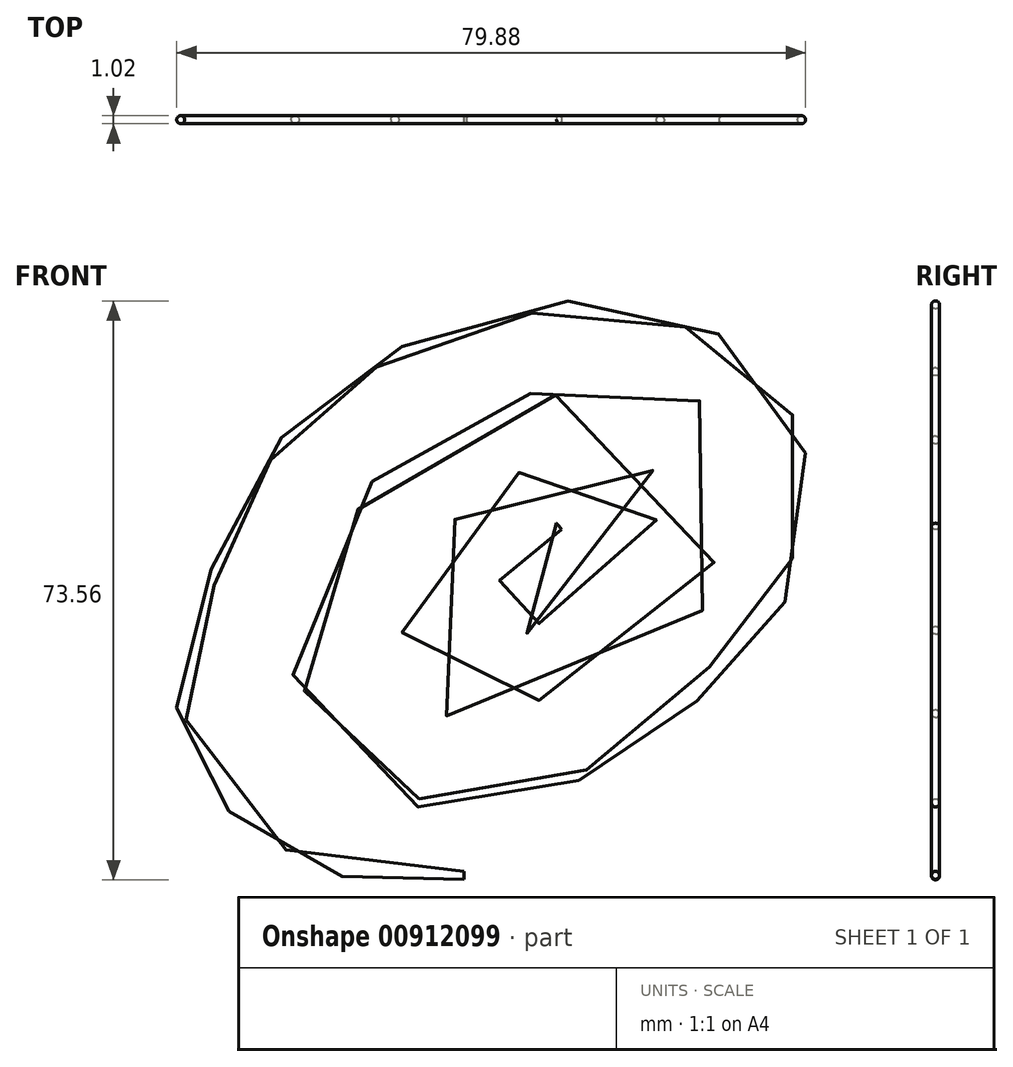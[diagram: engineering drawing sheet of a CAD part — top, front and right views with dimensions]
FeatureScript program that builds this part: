
annotation { "Feature Type Name" : "Feature", "Feature Type Description" : "" }
export const myFeature = defineFeature(function(context is Context, id is Id, definition is map)
    precondition{}
    {
        {
            var Q0;
            Q0=qCreatedBy(makeId("Front.planeOp"),FACE);
            var sketch = newSketch(context, id + "F0", { "sketchPlane" : qUnion([Q0])});
            skFitSpline(sketch, "E0", {"points": [v(-4.46, 18.28) * mm, v(-15.4, 6.19) * mm, v(5.32, 11.08) * mm, v(4.46, 28.06) * mm, v(-16.55, 19.71) * mm, v(-23.46, -3.3) * mm, v(8.2, 2.45) * mm, v(16.26, 22.3) * mm, v(9.35, 37.27) * mm, v(-5.61, 35.26) * mm, v(-17.12, 31.8) * mm, v(-32.1, 18.56) * mm, v(-37.85, 0) * mm, v(-28.64, -15.4) * mm, v(-15.97, -16.26) * mm, v(-4.75, -14.25) * mm, v(6.76, -9.93) * mm, v(11.66, -5.04) * mm, v(18.85, 5.04) * mm, v(22.88, 7.91) * mm, v(25.47, 13.1) * mm, v(26.33, 25.18) * mm, v(24.6, 34.97) * mm, v(15.69, 42.16) * mm, v(6.76, 45.62) * mm, v(-5.61, 46.2) * mm, v(-17.99, 43.03) * mm, v(-31.23, 36.98) * mm, v(-37.56, 30.94) * mm, v(-44.47, 23.46) * mm, v(-47.92, 13.67) * mm, v(-51.37, 2.73) * mm, v(-52.52, -4.46) * mm, v(-51.09, -10.22) * mm, v(-47.34, -15.69) * mm, v(-43.6, -20.3) * mm, v(-34.97, -25.18) * mm, v(-30.65, -25.76) * mm, v(-26.9, -26.05) * mm, v(-16.55, -26.05) * mm], "startDerivative": vector(-648.87, -504.58) * mm, "endDerivative": vector(493.43, 8.13) * mm});
            skSolve(sketch);
        }
        {
            var Q0;
            Q0=sQuery(id+"F0.wireOp",VERTEX,"E0.end");
            var Q1;
            Q1=sQuery(id+"F0.wireOp",EDGE,"E0");
            cPlane(context, id + "F1", {"entities" : qUnion([Q0, Q1]), "cplaneType" : CPlaneType.CURVE_POINT, "offset" : 25.4 * mm, "width" : 152.4 * mm, "height" : 152.4 * mm});
        }
        {
            var Q0;
            Q0=qCreatedBy(id+"F1.planeOp",FACE);
            var sketch = newSketch(context, id + "F2", { "sketchPlane" : qUnion([Q0])});
            skCircle(sketch, "E1", {"center": v(0, -25.77) * mm, "radius": 0.5 * mm});
            skSolve(sketch);
        }
        {
            var Q0;
            Q0=makeQuery(id+"F2.imprint","IMPRINT",FACE,{"disambiguationData":[TD([[makeQuery(id+"F2.imprint","IMPRINT",EDGE,{"derivedFrom":sQuery(id+"F2.wireOp",EDGE,"E1")}),1.0]])]});
            var Q1;
            Q1=sQuery(id+"F0.wireOp",EDGE,"E0");
            sweep(context, id + "F3", {"profiles" : qUnion([Q0]), "path" : qUnion([Q1])});
        }
    });
